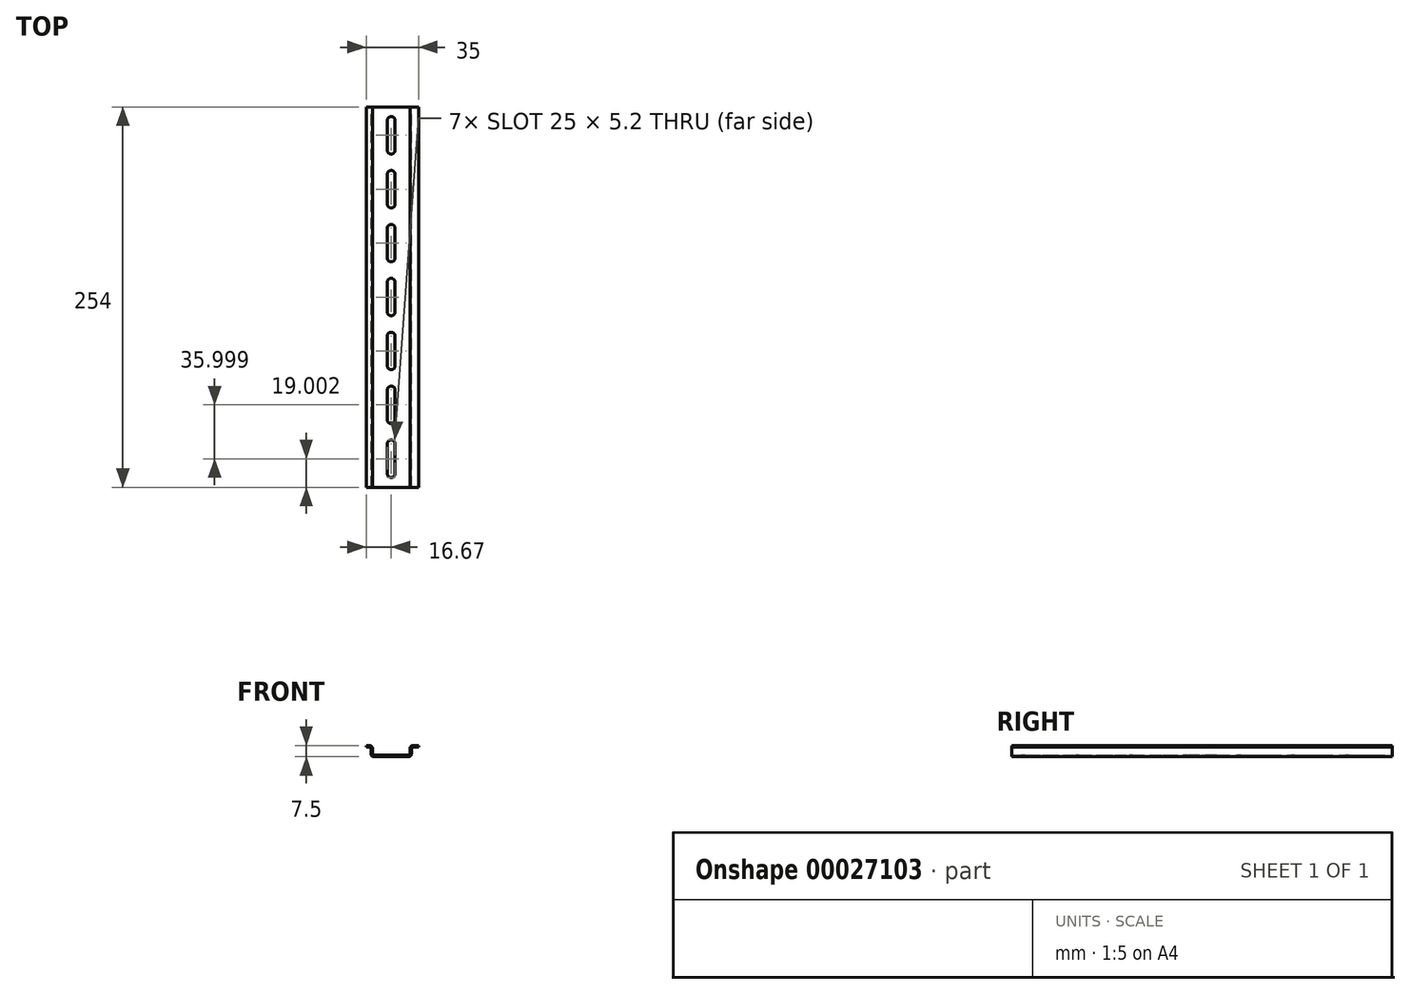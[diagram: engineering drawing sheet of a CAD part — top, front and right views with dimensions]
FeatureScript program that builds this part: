
annotation { "Feature Type Name" : "Feature", "Feature Type Description" : "" }
export const myFeature = defineFeature(function(context is Context, id is Id, definition is map)
    precondition{}
    {
        {
            var Q0;
            Q0=qCreatedBy(makeId("Front.planeOp"),FACE);
            var sketch = newSketch(context, id + "F0", { "sketchPlane" : qUnion([Q0])});
            skLineSegment(sketch, "E0", {"start": v(-11.5, 0) * mm, "end": v(11.5, 0) * mm});
            skLineSegment(sketch, "E1", {"start": v(13.5, 2) * mm, "end": v(13.5, 5.5) * mm});
            skLineSegment(sketch, "E2", {"start": v(14.5, 6.5) * mm, "end": v(18.33, 6.5) * mm});
            skLineSegment(sketch, "E3", {"start": v(18.33, 6.5) * mm, "end": v(18.33, 7.5) * mm});
            skLineSegment(sketch, "E4", {"start": v(18.33, 7.5) * mm, "end": v(14.52, 7.5) * mm});
            skLineSegment(sketch, "E5", {"start": v(12.52, 5.5) * mm, "end": v(12.52, 2) * mm});
            skLineSegment(sketch, "E6", {"start": v(11.52, 1) * mm, "end": v(-11.48, 1) * mm});
            skLineSegment(sketch, "E7", {"start": v(-12.48, 2) * mm, "end": v(-12.48, 5.5) * mm});
            skLineSegment(sketch, "E8", {"start": v(-14.48, 7.5) * mm, "end": v(-16.67, 7.5) * mm});
            skLineSegment(sketch, "E9", {"start": v(-16.67, 7.5) * mm, "end": v(-16.67, 6.5) * mm});
            skLineSegment(sketch, "E10", {"start": v(-16.67, 6.5) * mm, "end": v(-14.5, 6.5) * mm});
            skLineSegment(sketch, "E11", {"start": v(-13.5, 5.5) * mm, "end": v(-13.5, 2) * mm});
            skPoint(sketch, "E12.visualSharp", {"position": v(-12.48, 1) * mm});
            skArc(sketch, "E12.filletArc", {"start": v(-12.48, 2) * mm, "mid": v(-12.2, 1.3) * mm, "end": v(-11.48, 1) * mm});
            skPoint(sketch, "E13.visualSharp", {"position": v(12.52, 1) * mm});
            skArc(sketch, "E13.filletArc", {"start": v(11.52, 1) * mm, "mid": v(12.22, 1.3) * mm, "end": v(12.52, 2) * mm});
            skPoint(sketch, "E14.visualSharp", {"position": v(13.5, 6.5) * mm});
            skArc(sketch, "E14.filletArc", {"start": v(14.5, 6.5) * mm, "mid": v(13.8, 6.2) * mm, "end": v(13.5, 5.5) * mm});
            skPoint(sketch, "E15.visualSharp", {"position": v(-13.5, 6.5) * mm});
            skArc(sketch, "E15.filletArc", {"start": v(-13.5, 5.5) * mm, "mid": v(-13.8, 6.2) * mm, "end": v(-14.5, 6.5) * mm});
            skPoint(sketch, "E16.visualSharp", {"position": v(12.52, 7.5) * mm});
            skArc(sketch, "E16.filletArc", {"start": v(14.52, 7.5) * mm, "mid": v(13.1, 6.92) * mm, "end": v(12.52, 5.5) * mm});
            skPoint(sketch, "E17.visualSharp", {"position": v(13.5, 0) * mm});
            skArc(sketch, "E17.filletArc", {"start": v(11.5, 0) * mm, "mid": v(12.91, 0.59) * mm, "end": v(13.5, 2) * mm});
            skPoint(sketch, "E18.visualSharp", {"position": v(-13.5, 0) * mm});
            skArc(sketch, "E18.filletArc", {"start": v(-13.5, 2) * mm, "mid": v(-12.91, 0.59) * mm, "end": v(-11.5, 0) * mm});
            skPoint(sketch, "E19.visualSharp", {"position": v(-12.48, 7.5) * mm});
            skArc(sketch, "E19.filletArc", {"start": v(-12.48, 5.5) * mm, "mid": v(-13.07, 6.92) * mm, "end": v(-14.48, 7.5) * mm});
            skSolve(sketch);
        }
        {
            var Q0;
            Q0 = qSketchRegion(id + "F0", true);
            extrude(context, id + "F1", {"entities" : qUnion([Q0]), "endBound" : BoundingType.SYMMETRIC, "depth" : 254 * mm});
        }
        {
            var Q0;
            Q0=makeQuery(id+"F1.opExtrude","SWEPT_FACE",FACE,{"disambiguationData":[OSD([sQuery(id+"F0.wireOp",EDGE,"E6")])]});
            var sketch = newSketch(context, id + "F2", { "sketchPlane" : qUnion([Q0])});
            skLineSegment(sketch, "E20", {"start": v(-2.6, 9.9) * mm, "end": v(-2.6, -9.9) * mm});
            skArc(sketch, "E21", {"start": v(-2.6, -9.9) * mm, "mid": v(0, -12.5) * mm, "end": v(2.6, -9.9) * mm});
            skLineSegment(sketch, "E22", {"start": v(2.6, -9.9) * mm, "end": v(2.6, 9.9) * mm});
            skArc(sketch, "E23", {"start": v(2.6, 9.9) * mm, "mid": v(0, 12.5) * mm, "end": v(-2.6, 9.9) * mm});
            skLineSegment(sketch, "E24", {"start": v(2.6, 26.1) * mm, "end": v(2.6, 45.9) * mm});
            skLineSegment(sketch, "E25", {"start": v(-2.6, 45.9) * mm, "end": v(-2.6, 26.1) * mm});
            skArc(sketch, "E26", {"start": v(2.6, 45.9) * mm, "mid": v(0, 48.5) * mm, "end": v(-2.6, 45.9) * mm});
            skArc(sketch, "E27", {"start": v(-2.6, 26.1) * mm, "mid": v(0, 23.5) * mm, "end": v(2.6, 26.1) * mm});
            skLineSegment(sketch, "E28", {"start": v(2.6, 62.1) * mm, "end": v(2.6, 81.9) * mm});
            skLineSegment(sketch, "E29", {"start": v(-2.6, 81.9) * mm, "end": v(-2.6, 62.1) * mm});
            skArc(sketch, "E30", {"start": v(2.6, 81.9) * mm, "mid": v(0, 84.5) * mm, "end": v(-2.6, 81.9) * mm});
            skArc(sketch, "E31", {"start": v(-2.6, 62.1) * mm, "mid": v(0, 59.5) * mm, "end": v(2.6, 62.1) * mm});
            skLineSegment(sketch, "E32", {"start": v(2.6, 98.1) * mm, "end": v(2.6, 117.9) * mm});
            skLineSegment(sketch, "E33", {"start": v(-2.6, 117.9) * mm, "end": v(-2.6, 98.1) * mm});
            skArc(sketch, "E34", {"start": v(2.6, 117.9) * mm, "mid": v(0, 120.5) * mm, "end": v(-2.6, 117.9) * mm});
            skArc(sketch, "E35", {"start": v(-2.6, 98.1) * mm, "mid": v(0, 95.5) * mm, "end": v(2.6, 98.1) * mm});
            skLineSegment(sketch, "E36", {"start": v(2.6, -45.9) * mm, "end": v(2.6, -26.1) * mm});
            skLineSegment(sketch, "E37", {"start": v(-2.6, -26.1) * mm, "end": v(-2.6, -45.9) * mm});
            skArc(sketch, "E38", {"start": v(2.6, -26.1) * mm, "mid": v(0, -23.5) * mm, "end": v(-2.6, -26.1) * mm});
            skArc(sketch, "E39", {"start": v(-2.6, -45.9) * mm, "mid": v(0, -48.5) * mm, "end": v(2.6, -45.9) * mm});
            skLineSegment(sketch, "E40", {"start": v(2.6, -81.9) * mm, "end": v(2.6, -62.1) * mm});
            skLineSegment(sketch, "E41", {"start": v(-2.6, -62.1) * mm, "end": v(-2.6, -81.9) * mm});
            skArc(sketch, "E42", {"start": v(2.6, -62.1) * mm, "mid": v(0, -59.5) * mm, "end": v(-2.6, -62.1) * mm});
            skArc(sketch, "E43", {"start": v(-2.6, -81.9) * mm, "mid": v(0, -84.5) * mm, "end": v(2.6, -81.9) * mm});
            skLineSegment(sketch, "E44", {"start": v(2.6, -117.9) * mm, "end": v(2.6, -98.1) * mm});
            skLineSegment(sketch, "E45", {"start": v(-2.6, -98.1) * mm, "end": v(-2.6, -117.9) * mm});
            skArc(sketch, "E46", {"start": v(2.6, -98.1) * mm, "mid": v(0, -95.5) * mm, "end": v(-2.6, -98.1) * mm});
            skArc(sketch, "E47", {"start": v(-2.6, -117.9) * mm, "mid": v(0, -120.5) * mm, "end": v(2.6, -117.9) * mm});
            skSolve(sketch);
        }
        {
            var Q0;
            Q0 = qSketchRegion(id + "F2", true);
            extrude(context, id + "F3", {"entities" : qUnion([Q0]), "operationType" : NewBodyOperationType.REMOVE, "endBound" : BoundingType.THROUGH_ALL, "oppositeDirection" : true, "depth" : 25.4 * mm});
        }
    });
